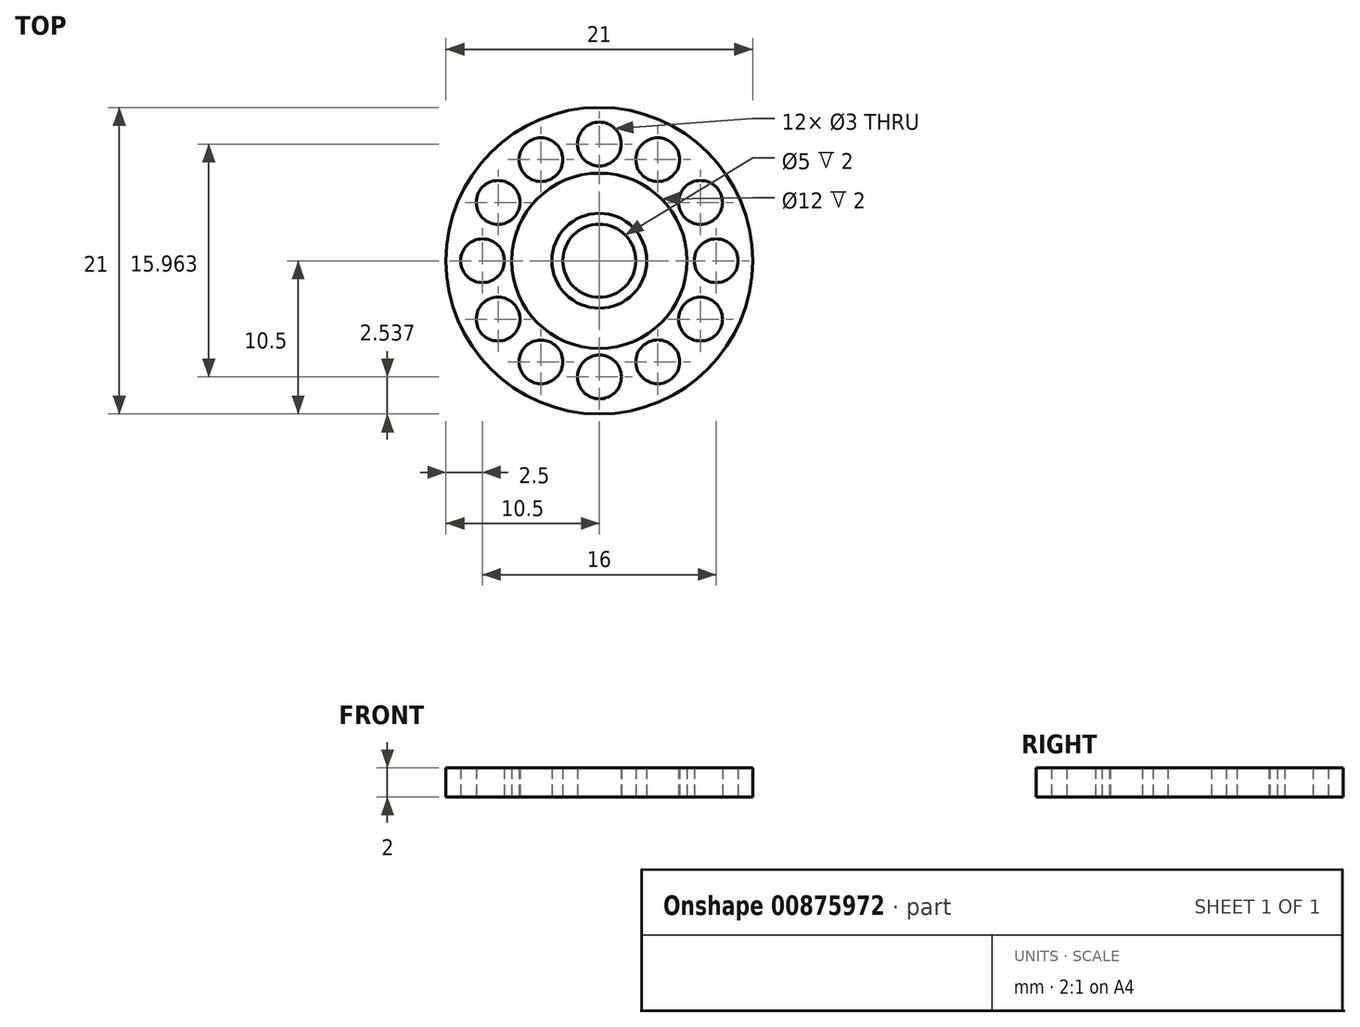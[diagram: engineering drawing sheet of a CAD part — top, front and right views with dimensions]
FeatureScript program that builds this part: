
annotation { "Feature Type Name" : "Feature", "Feature Type Description" : "" }
export const myFeature = defineFeature(function(context is Context, id is Id, definition is map)
    precondition{}
    {
        {
            var Q0;
            Q0=qCreatedBy(makeId("Top.planeOp"),FACE);
            var sketch = newSketch(context, id + "F0", { "sketchPlane" : qUnion([Q0])});
            skCircle(sketch, "E0", {"center": v(0, 0) * mm, "radius": 2.5 * mm});
            skCircle(sketch, "E1", {"center": v(-4, 6.93) * mm, "radius": 1.5 * mm});
            skCircle(sketch, "E2", {"center": v(-8, 0) * mm, "radius": 1.5 * mm});
            skCircle(sketch, "E3", {"center": v(-6.93, 4) * mm, "radius": 1.5 * mm});
            skCircle(sketch, "E4", {"center": v(0, 8) * mm, "radius": 1.5 * mm});
            skCircle(sketch, "E5", {"center": v(6.93, 4) * mm, "radius": 1.5 * mm});
            skCircle(sketch, "E6", {"center": v(4, 6.93) * mm, "radius": 1.5 * mm});
            skCircle(sketch, "E7", {"center": v(8, 0) * mm, "radius": 1.5 * mm});
            skLineSegment(sketch, "E8.0", {"start": v(8, 0) * mm, "end": v(6.93, -4) * mm});
            skLineSegment(sketch, "E8.1", {"start": v(6.93, -4) * mm, "end": v(4, -6.93) * mm});
            skLineSegment(sketch, "E8.2", {"start": v(4, -6.93) * mm, "end": v(0, -8) * mm});
            skLineSegment(sketch, "E8.3", {"start": v(0, -8) * mm, "end": v(-4, -6.93) * mm});
            skLineSegment(sketch, "E8.4", {"start": v(-4, -6.93) * mm, "end": v(-6.93, -4) * mm});
            skLineSegment(sketch, "E8.5", {"start": v(-6.93, -4) * mm, "end": v(-8, 0) * mm});
            skLineSegment(sketch, "E8.6", {"start": v(-8, 0) * mm, "end": v(-6.93, 4) * mm});
            skLineSegment(sketch, "E8.7", {"start": v(-6.93, 4) * mm, "end": v(-4, 6.93) * mm});
            skLineSegment(sketch, "E8.8", {"start": v(-4, 6.93) * mm, "end": v(0, 8) * mm});
            skLineSegment(sketch, "E8.9", {"start": v(0, 8) * mm, "end": v(4, 6.93) * mm});
            skLineSegment(sketch, "E8.10", {"start": v(4, 6.93) * mm, "end": v(6.93, 4) * mm});
            skLineSegment(sketch, "E8.11", {"start": v(6.93, 4) * mm, "end": v(8, 0) * mm});
            skCircle(sketch, "E9", {"center": v(-6.93, -4) * mm, "radius": 1.5 * mm});
            skCircle(sketch, "E10", {"center": v(-4, -6.93) * mm, "radius": 1.5 * mm});
            skCircle(sketch, "E11", {"center": v(0.01, -7.96) * mm, "radius": 1.5 * mm});
            skCircle(sketch, "E12", {"center": v(4, -6.93) * mm, "radius": 1.5 * mm});
            skCircle(sketch, "E13", {"center": v(6.93, -4) * mm, "radius": 1.5 * mm});
            skCircle(sketch, "E14", {"center": v(0, 0) * mm, "radius": 10.5 * mm});
            skCircle(sketch, "E15", {"center": v(0, 0) * mm, "radius": 3.25 * mm});
            skCircle(sketch, "E16", {"center": v(0, 0) * mm, "radius": 6 * mm});
            skSolve(sketch);
        }
        {
            var Q0;
            Q0=makeQuery(id+"F0.imprint","IMPRINT",FACE,{"disambiguationData":[TD([[makeQuery(id+"F0.imprint","IMPRINT",EDGE,{"derivedFrom":sQuery(id+"F0.wireOp",EDGE,"E14")}),1.0]])]});
            var Q1;
            Q1=makeQuery(id+"F0.imprint","IMPRINT",FACE,{"disambiguationData":[TD([[makeQuery(id+"F0.imprint","IMPRINT",EDGE,{"derivedFrom":sQuery(id+"F0.wireOp",EDGE,"E16")}),-1.0]])]});
            var Q2;
            Q2=makeQuery(id+"F0.imprint","IMPRINT",FACE,{"disambiguationData":[TD([[makeQuery(id+"F0.imprint","IMPRINT",EDGE,{"derivedFrom":sQuery(id+"F0.wireOp",EDGE,"E0")}),-1.0]])]});
            extrude(context, id + "F1", {"entities" : qUnion([Q0, Q1, Q2]), "depth" : 2 * mm, "offsetDistance" : 25 * mm});
        }
        {
            var Q0;
            Q0=qCreatedBy(makeId("Top.planeOp"),FACE);
            var sketch = newSketch(context, id + "F2", { "sketchPlane" : qUnion([Q0])});
            skCircle(sketch, "E17", {"center": v(0, 0) * mm, "radius": 11 * mm});
            skSolve(sketch);
        }
        {
            var Q0;
            Q0=sQuery(id+"F2.wireOp",EDGE,"E17");
            extrude(context, id + "F3", {"bodyType" : ToolBodyType.SURFACE, "surfaceEntities" : qUnion([Q0]), "depth" : 25 * mm, "offsetDistance" : 25 * mm});
        }
    });
